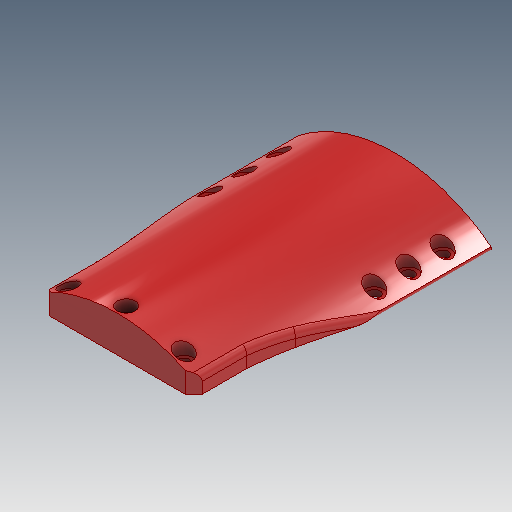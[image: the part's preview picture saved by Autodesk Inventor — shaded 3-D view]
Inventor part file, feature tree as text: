
AUTODESK INVENTOR PART (.ipt)
format: ipt  version: 2020.3 (Build 243373010, 373A)  size: 355,328 bytes
history: native  units: mm
features: extrude x6, sketch x3, mirror x2, plane x1, chamfer x1, fillet x1, pattern_linear x1
ambient origin geometry x8: Origin, YZ Plane, XZ Plane, XY Plane, X Axis, Y Axis, Z Axis, Center Point
bodies: Solid1 (feature_tree)
feature tree (15):
  extrude  "Extrusion1"  Depth=325.038mm TaperAngle=0.0deg
  extrude  "Extrusion2"  [1 undecoded]
  mirror  "Mirror1"
  plane  "Work Plane1"
  extrude  "Extrusion3"  Depth=10.0mm TaperAngle=45.0deg
  chamfer  "Chamfer2"  Distance=2.0mm
  fillet  "Fillet2"  Radius=10.0mm
  sketch  "Sketch6"  dims[d7=42.508mm d8=0.0mm d12=10.0mm d13=2.0mm d14=45.0deg d16=2.0mm d17=10.0mm d37=21.0mm d38=14.196mm d39=0.0mm d40=21.0mm d41=21.0mm d42=21.0mm d43=21.0mm d44=30.0mm d46=40.0mm d47=10.0mm d49=10.0mm d51=23.846mm d52=0.0mm d53=35.213mm d54=0.0mm d55=30.0mm d57=40.0mm]
  extrude  "Extrusion4"  Depth=10.0mm
  extrude  "Extrusion5"  Depth=10.0mm TaperAngle=0.0deg
  extrude  "Extrusion6"  Depth=10.0mm
  mirror  "Mirror2"
  pattern_linear  "Rectangular Pattern1"  Spacing1=21.0mm  [1 undecoded]
  sketch  "Sketch2"  dims[d0=234.147mm d2=325.038mm d3=0.0mm]
  sketch  "Sketch3"  dims[d4=0.0mm d5=0.0mm d6=-42.5mm]
note: 2 required parameter values undecoded (feature->parameter linkage not recoverable at this tier; creation-order binding heuristic only, values carry confidence <= 0.55)
